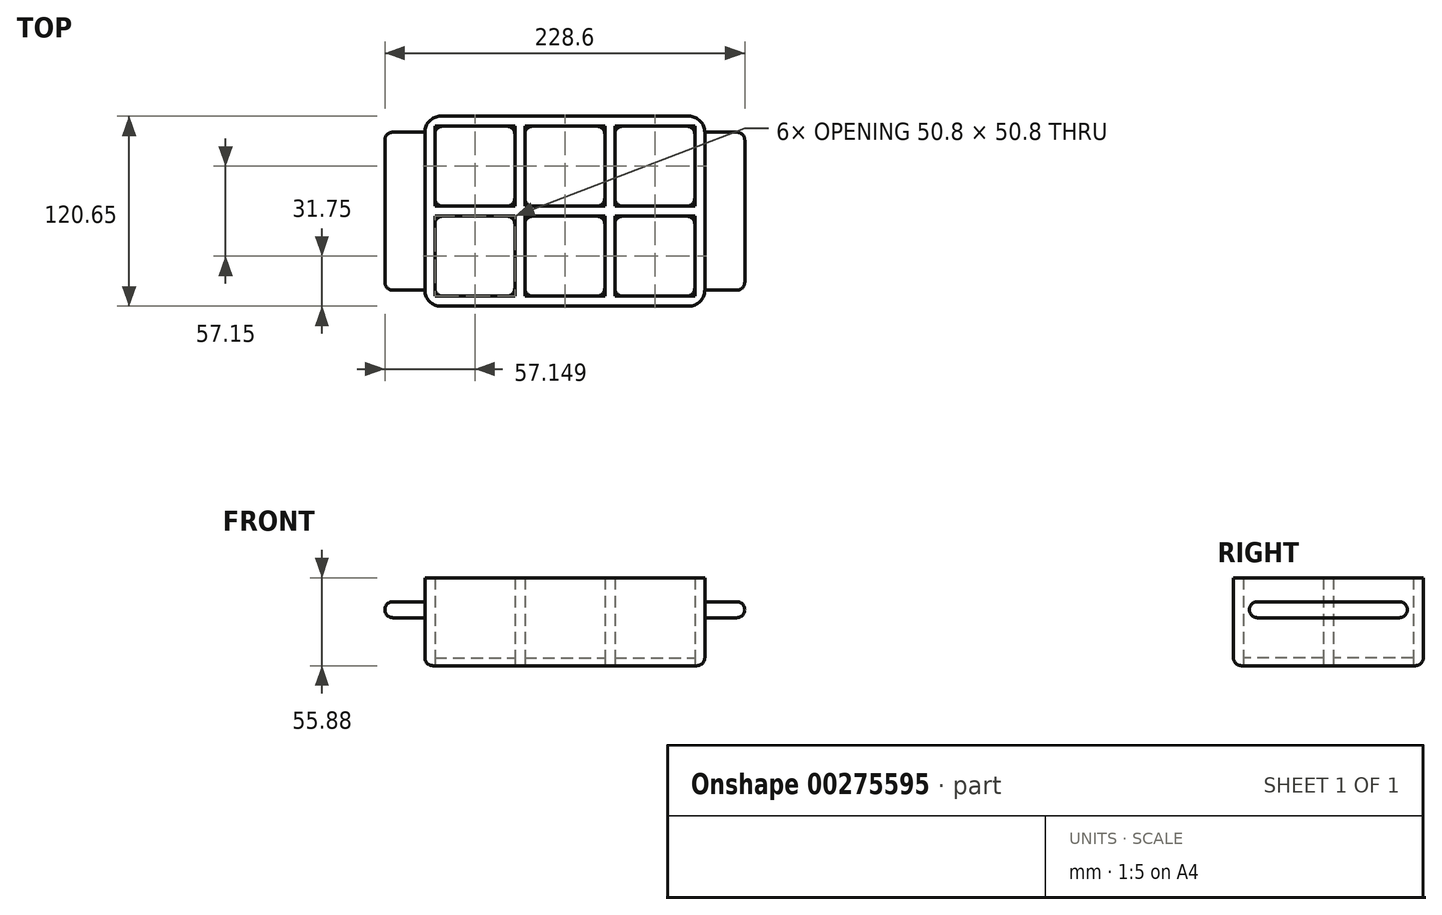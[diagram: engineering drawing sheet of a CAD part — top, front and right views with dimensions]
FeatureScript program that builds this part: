
annotation { "Feature Type Name" : "Feature", "Feature Type Description" : "" }
export const myFeature = defineFeature(function(context is Context, id is Id, definition is map)
    precondition{}
    {
        {
            var Q0;
            Q0=qCreatedBy(makeId("Top.planeOp"),FACE);
            var sketch = newSketch(context, id + "F0", { "sketchPlane" : qUnion([Q0])});
            skLineSegment(sketch, "E0.bottom", {"start": v(-74.45, 57.15) * mm, "end": v(103.35, 57.15) * mm});
            skLineSegment(sketch, "E0.top", {"start": v(-74.45, -63.5) * mm, "end": v(103.35, -63.5) * mm});
            skLineSegment(sketch, "E0.left", {"start": v(-74.45, 57.15) * mm, "end": v(-74.45, -63.5) * mm});
            skLineSegment(sketch, "E0.right", {"start": v(103.35, 57.15) * mm, "end": v(103.35, -63.5) * mm});
            skLineSegment(sketch, "E1.bottom", {"start": v(-68.1, 50.8) * mm, "end": v(-17.3, 50.8) * mm});
            skLineSegment(sketch, "E1.top", {"start": v(-68.1, 0) * mm, "end": v(-17.3, 0) * mm});
            skLineSegment(sketch, "E1.left", {"start": v(-68.1, 50.8) * mm, "end": v(-68.1, 0) * mm});
            skLineSegment(sketch, "E1.right", {"start": v(-17.3, 50.8) * mm, "end": v(-17.3, 0) * mm});
            skLineSegment(sketch, "E2.bottom", {"start": v(-68.1, -6.35) * mm, "end": v(-17.3, -6.35) * mm});
            skLineSegment(sketch, "E2.top", {"start": v(-68.1, -57.15) * mm, "end": v(-17.3, -57.15) * mm});
            skLineSegment(sketch, "E2.left", {"start": v(-68.1, -6.35) * mm, "end": v(-68.1, -57.15) * mm});
            skLineSegment(sketch, "E2.right", {"start": v(-17.3, -6.35) * mm, "end": v(-17.3, -57.15) * mm});
            skLineSegment(sketch, "E3.bottom", {"start": v(-10.95, 50.8) * mm, "end": v(39.85, 50.8) * mm});
            skLineSegment(sketch, "E3.top", {"start": v(-10.95, 0) * mm, "end": v(39.85, 0) * mm});
            skLineSegment(sketch, "E3.left", {"start": v(-10.95, 50.8) * mm, "end": v(-10.95, 0) * mm});
            skLineSegment(sketch, "E3.right", {"start": v(39.85, 50.8) * mm, "end": v(39.85, 0) * mm});
            skLineSegment(sketch, "E4.bottom", {"start": v(-10.95, -6.35) * mm, "end": v(39.85, -6.35) * mm});
            skLineSegment(sketch, "E4.top", {"start": v(-10.95, -57.15) * mm, "end": v(39.85, -57.15) * mm});
            skLineSegment(sketch, "E4.left", {"start": v(-10.95, -6.35) * mm, "end": v(-10.95, -57.15) * mm});
            skLineSegment(sketch, "E4.right", {"start": v(39.85, -6.35) * mm, "end": v(39.85, -57.15) * mm});
            skLineSegment(sketch, "E5.bottom", {"start": v(46.2, 50.8) * mm, "end": v(97, 50.8) * mm});
            skLineSegment(sketch, "E5.top", {"start": v(46.2, 0) * mm, "end": v(97, 0) * mm});
            skLineSegment(sketch, "E5.left", {"start": v(46.2, 50.8) * mm, "end": v(46.2, 0) * mm});
            skLineSegment(sketch, "E5.right", {"start": v(97, 50.8) * mm, "end": v(97, 0) * mm});
            skLineSegment(sketch, "E6.bottom", {"start": v(46.2, -6.35) * mm, "end": v(97, -6.35) * mm});
            skLineSegment(sketch, "E6.top", {"start": v(46.2, -57.15) * mm, "end": v(97, -57.15) * mm});
            skLineSegment(sketch, "E6.left", {"start": v(46.2, -6.35) * mm, "end": v(46.2, -57.15) * mm});
            skLineSegment(sketch, "E6.right", {"start": v(97, -6.35) * mm, "end": v(97, -57.15) * mm});
            skSolve(sketch);
        }
        {
            var Q0;
            Q0=makeQuery(id+"F0.imprint","IMPRINT",FACE,{"disambiguationData":[TD([[makeQuery(id+"F0.imprint","IMPRINT",EDGE,{"derivedFrom":sQuery(id+"F0.wireOp",EDGE,"E6.bottom")}),-1.0]])]});
            var Q1;
            Q1=makeQuery(id+"F0.imprint","IMPRINT",FACE,{"disambiguationData":[TD([[makeQuery(id+"F0.imprint","IMPRINT",EDGE,{"derivedFrom":sQuery(id+"F0.wireOp",EDGE,"E4.bottom")}),-1.0]])]});
            var Q2;
            Q2=makeQuery(id+"F0.imprint","IMPRINT",FACE,{"disambiguationData":[TD([[makeQuery(id+"F0.imprint","IMPRINT",EDGE,{"derivedFrom":sQuery(id+"F0.wireOp",EDGE,"E2.bottom")}),-1.0]])]});
            var Q3;
            Q3=makeQuery(id+"F0.imprint","IMPRINT",FACE,{"disambiguationData":[TD([[makeQuery(id+"F0.imprint","IMPRINT",EDGE,{"derivedFrom":sQuery(id+"F0.wireOp",EDGE,"E1.bottom")}),-1.0]])]});
            var Q4;
            Q4=makeQuery(id+"F0.imprint","IMPRINT",FACE,{"disambiguationData":[TD([[makeQuery(id+"F0.imprint","IMPRINT",EDGE,{"derivedFrom":sQuery(id+"F0.wireOp",EDGE,"E3.bottom")}),-1.0]])]});
            var Q5;
            Q5=makeQuery(id+"F0.imprint","IMPRINT",FACE,{"disambiguationData":[TD([[makeQuery(id+"F0.imprint","IMPRINT",EDGE,{"derivedFrom":sQuery(id+"F0.wireOp",EDGE,"E5.bottom")}),-1.0]])]});
            extrude(context, id + "F1", {"entities" : qUnion([Q0, Q1, Q2, Q3, Q4, Q5]), "depth" : 5.08 * mm});
        }
        {
            var Q0;
            Q0 = qSketchRegion(id + "F0", true);
            extrude(context, id + "F2", {"entities" : qUnion([Q0]), "depth" : 55.88 * mm});
        }
        {
            var Q0;
            Q0=makeQuery(id+"F2.opExtrude","SWEPT_EDGE",EDGE,{"disambiguationData":[OSD([sQuery(id+"F0.wireOp",EDGE,"E0.top"),sQuery(id+"F0.wireOp",EDGE,"E0.right")])]});
            var Q1;
            Q1=makeQuery(id+"F2.opExtrude","SWEPT_EDGE",EDGE,{"disambiguationData":[OSD([sQuery(id+"F0.wireOp",EDGE,"E0.bottom"),sQuery(id+"F0.wireOp",EDGE,"E0.right")])]});
            var Q2;
            Q2=makeQuery(id+"F2.opExtrude","SWEPT_EDGE",EDGE,{"disambiguationData":[OSD([sQuery(id+"F0.wireOp",EDGE,"E0.bottom"),sQuery(id+"F0.wireOp",EDGE,"E0.left")])]});
            var Q3;
            Q3=makeQuery(id+"F2.opExtrude","SWEPT_EDGE",EDGE,{"disambiguationData":[OSD([sQuery(id+"F0.wireOp",EDGE,"E0.top"),sQuery(id+"F0.wireOp",EDGE,"E0.left")])]});
            fillet(context, id + "F3", {"entities" : qUnion([Q0, Q1, Q2, Q3]), "radius" : 10.16 * mm, "tangentPropagation" : true, "allowEdgeOverflow" : false});
        }
        {
            var Q0;
            Q0=makeQuery(id+"F2.opExtrude","SWEPT_EDGE",EDGE,{"disambiguationData":[OSD([sQuery(id+"F0.wireOp",EDGE,"E2.bottom"),sQuery(id+"F0.wireOp",EDGE,"E2.right")])]});
            var Q1;
            Q1=makeQuery(id+"F2.opExtrude","SWEPT_EDGE",EDGE,{"disambiguationData":[OSD([sQuery(id+"F0.wireOp",EDGE,"E1.bottom"),sQuery(id+"F0.wireOp",EDGE,"E1.right")])]});
            var Q2;
            Q2=makeQuery(id+"F2.opExtrude","SWEPT_EDGE",EDGE,{"disambiguationData":[OSD([sQuery(id+"F0.wireOp",EDGE,"E3.bottom"),sQuery(id+"F0.wireOp",EDGE,"E3.right")])]});
            var Q3;
            Q3=makeQuery(id+"F2.opExtrude","SWEPT_EDGE",EDGE,{"disambiguationData":[OSD([sQuery(id+"F0.wireOp",EDGE,"E5.bottom"),sQuery(id+"F0.wireOp",EDGE,"E5.right")])]});
            var Q4;
            Q4=makeQuery(id+"F2.opExtrude","SWEPT_EDGE",EDGE,{"disambiguationData":[OSD([sQuery(id+"F0.wireOp",EDGE,"E6.bottom"),sQuery(id+"F0.wireOp",EDGE,"E6.right")])]});
            var Q5;
            Q5=makeQuery(id+"F2.opExtrude","SWEPT_EDGE",EDGE,{"disambiguationData":[OSD([sQuery(id+"F0.wireOp",EDGE,"E4.bottom"),sQuery(id+"F0.wireOp",EDGE,"E4.right")])]});
            var Q6;
            Q6=makeQuery(id+"F2.opExtrude","SWEPT_EDGE",EDGE,{"disambiguationData":[OSD([sQuery(id+"F0.wireOp",EDGE,"E5.top"),sQuery(id+"F0.wireOp",EDGE,"E5.right")])]});
            var Q7;
            Q7=makeQuery(id+"F2.opExtrude","SWEPT_EDGE",EDGE,{"disambiguationData":[OSD([sQuery(id+"F0.wireOp",EDGE,"E3.top"),sQuery(id+"F0.wireOp",EDGE,"E3.right")])]});
            var Q8;
            Q8=makeQuery(id+"F2.opExtrude","SWEPT_EDGE",EDGE,{"disambiguationData":[OSD([sQuery(id+"F0.wireOp",EDGE,"E1.top"),sQuery(id+"F0.wireOp",EDGE,"E1.right")])]});
            var Q9;
            Q9=makeQuery(id+"F2.opExtrude","SWEPT_EDGE",EDGE,{"disambiguationData":[OSD([sQuery(id+"F0.wireOp",EDGE,"E2.top"),sQuery(id+"F0.wireOp",EDGE,"E2.right")])]});
            var Q10;
            Q10=makeQuery(id+"F2.opExtrude","SWEPT_EDGE",EDGE,{"disambiguationData":[OSD([sQuery(id+"F0.wireOp",EDGE,"E4.top"),sQuery(id+"F0.wireOp",EDGE,"E4.right")])]});
            var Q11;
            Q11=makeQuery(id+"F2.opExtrude","SWEPT_EDGE",EDGE,{"disambiguationData":[OSD([sQuery(id+"F0.wireOp",EDGE,"E6.top"),sQuery(id+"F0.wireOp",EDGE,"E6.right")])]});
            var Q12;
            Q12=makeQuery(id+"F2.opExtrude","SWEPT_EDGE",EDGE,{"disambiguationData":[OSD([sQuery(id+"F0.wireOp",EDGE,"E6.top"),sQuery(id+"F0.wireOp",EDGE,"E6.left")])]});
            var Q13;
            Q13=makeQuery(id+"F2.opExtrude","SWEPT_EDGE",EDGE,{"disambiguationData":[OSD([sQuery(id+"F0.wireOp",EDGE,"E5.top"),sQuery(id+"F0.wireOp",EDGE,"E5.left")])]});
            var Q14;
            Q14=makeQuery(id+"F2.opExtrude","SWEPT_EDGE",EDGE,{"disambiguationData":[OSD([sQuery(id+"F0.wireOp",EDGE,"E4.top"),sQuery(id+"F0.wireOp",EDGE,"E4.left")])]});
            var Q15;
            Q15=makeQuery(id+"F2.opExtrude","SWEPT_EDGE",EDGE,{"disambiguationData":[OSD([sQuery(id+"F0.wireOp",EDGE,"E3.top"),sQuery(id+"F0.wireOp",EDGE,"E3.left")])]});
            var Q16;
            Q16=makeQuery(id+"F2.opExtrude","SWEPT_EDGE",EDGE,{"disambiguationData":[OSD([sQuery(id+"F0.wireOp",EDGE,"E1.top"),sQuery(id+"F0.wireOp",EDGE,"E1.left")])]});
            var Q17;
            Q17=makeQuery(id+"F2.opExtrude","SWEPT_EDGE",EDGE,{"disambiguationData":[OSD([sQuery(id+"F0.wireOp",EDGE,"E2.top"),sQuery(id+"F0.wireOp",EDGE,"E2.left")])]});
            var Q18;
            Q18=makeQuery(id+"F2.opExtrude","SWEPT_EDGE",EDGE,{"disambiguationData":[OSD([sQuery(id+"F0.wireOp",EDGE,"E6.bottom"),sQuery(id+"F0.wireOp",EDGE,"E6.left")])]});
            var Q19;
            Q19=makeQuery(id+"F2.opExtrude","SWEPT_EDGE",EDGE,{"disambiguationData":[OSD([sQuery(id+"F0.wireOp",EDGE,"E5.bottom"),sQuery(id+"F0.wireOp",EDGE,"E5.left")])]});
            var Q20;
            Q20=makeQuery(id+"F2.opExtrude","SWEPT_EDGE",EDGE,{"disambiguationData":[OSD([sQuery(id+"F0.wireOp",EDGE,"E3.bottom"),sQuery(id+"F0.wireOp",EDGE,"E3.left")])]});
            var Q21;
            Q21=makeQuery(id+"F2.opExtrude","SWEPT_EDGE",EDGE,{"disambiguationData":[OSD([sQuery(id+"F0.wireOp",EDGE,"E4.bottom"),sQuery(id+"F0.wireOp",EDGE,"E4.left")])]});
            var Q22;
            Q22=makeQuery(id+"F2.opExtrude","SWEPT_EDGE",EDGE,{"disambiguationData":[OSD([sQuery(id+"F0.wireOp",EDGE,"E2.bottom"),sQuery(id+"F0.wireOp",EDGE,"E2.left")])]});
            var Q23;
            Q23=makeQuery(id+"F2.opExtrude","SWEPT_EDGE",EDGE,{"disambiguationData":[OSD([sQuery(id+"F0.wireOp",EDGE,"E1.bottom"),sQuery(id+"F0.wireOp",EDGE,"E1.left")])]});
            var Q24;
            Q24=makeQuery(id+"F2.opExtrude","CAP_EDGE",EDGE,{"disambiguationData":[OSD([sQuery(id+"F0.wireOp",EDGE,"E0.right")])],"isStart":true});
            var Q25;
            Q25=makeQuery(id+"F2.opExtrude","CAP_EDGE",EDGE,{"disambiguationData":[OSD([sQuery(id+"F0.wireOp",EDGE,"E0.top")])],"isStart":true});
            fillet(context, id + "F4", {"entities" : qUnion([Q0, Q1, Q2, Q3, Q4, Q5, Q6, Q7, Q8, Q9, Q10, Q11, Q12, Q13, Q14, Q15, Q16, Q17, Q18, Q19, Q20, Q21, Q22, Q23, Q24, Q25]), "radius" : 5.08 * mm, "tangentPropagation" : true, "allowEdgeOverflow" : false});
        }
        {
            var Q0;
            Q0=makeQuery(id+"F2.opExtrude","SWEPT_FACE",FACE,{"disambiguationData":[OSD([sQuery(id+"F0.wireOp",EDGE,"E0.right")])]});
            var sketch = newSketch(context, id + "F5", { "sketchPlane" : qUnion([Q0])});
            skLineSegment(sketch, "E7.bottom", {"start": v(-53.34, 30.48) * mm, "end": v(47, 30.48) * mm});
            skLineSegment(sketch, "E7.top", {"start": v(-53.34, 40.64) * mm, "end": v(47, 40.64) * mm});
            skLineSegment(sketch, "E7.left", {"start": v(-53.34, 30.48) * mm, "end": v(-53.34, 40.64) * mm});
            skLineSegment(sketch, "E7.right", {"start": v(46.99, 30.48) * mm, "end": v(46.99, 40.64) * mm});
            skSolve(sketch);
        }
        {
            var Q0;
            Q0=makeQuery(id+"F5.imprint","IMPRINT",FACE,{"disambiguationData":[TD([[makeQuery(id+"F5.imprint","IMPRINT",EDGE,{"derivedFrom":sQuery(id+"F5.wireOp",EDGE,"E7.bottom")}),1.0]])]});
            extrude(context, id + "F6", {"entities" : qUnion([Q0]), "operationType" : NewBodyOperationType.ADD, "depth" : 25.4 * mm});
        }
        {
            var Q0;
            Q0=makeQuery(id+"F6.opExtrude","CAP_EDGE",EDGE,{"disambiguationData":[OSD([sQuery(id+"F5.wireOp",EDGE,"E7.top")])],"isStart":false});
            var Q1;
            Q1=makeQuery(id+"F6.opExtrude","SWEPT_EDGE",EDGE,{"disambiguationData":[OSD([sQuery(id+"F0.wireOp",EDGE,"E0.top"),sQuery(id+"F0.wireOp",EDGE,"E0.right"),sQuery(id+"F5.wireOp",EDGE,"E7.top"),sQuery(id+"F5.wireOp",EDGE,"E7.left")])]});
            var Q2;
            Q2=makeQuery(id+"F6.opExtrude","CAP_EDGE",EDGE,{"disambiguationData":[OSD([sQuery(id+"F5.wireOp",EDGE,"E7.left")])],"isStart":false});
            var Q3;
            Q3=makeQuery(id+"F6.opExtrude","SWEPT_EDGE",EDGE,{"disambiguationData":[OSD([sQuery(id+"F0.wireOp",EDGE,"E0.top"),sQuery(id+"F0.wireOp",EDGE,"E0.right"),sQuery(id+"F5.wireOp",EDGE,"E7.bottom"),sQuery(id+"F5.wireOp",EDGE,"E7.left")])]});
            var Q4;
            Q4=makeQuery(id+"F6.opExtrude","CAP_EDGE",EDGE,{"disambiguationData":[OSD([sQuery(id+"F5.wireOp",EDGE,"E7.bottom")])],"isStart":false});
            var Q5;
            Q5=makeQuery(id+"F6.opExtrude","SWEPT_EDGE",EDGE,{"disambiguationData":[OSD([sQuery(id+"F0.wireOp",EDGE,"E0.bottom"),sQuery(id+"F0.wireOp",EDGE,"E0.right"),sQuery(id+"F5.wireOp",EDGE,"E7.top"),sQuery(id+"F5.wireOp",EDGE,"E7.right")])]});
            var Q6;
            Q6=makeQuery(id+"F6.opExtrude","SWEPT_EDGE",EDGE,{"disambiguationData":[OSD([sQuery(id+"F0.wireOp",EDGE,"E0.bottom"),sQuery(id+"F0.wireOp",EDGE,"E0.right"),sQuery(id+"F5.wireOp",EDGE,"E7.bottom"),sQuery(id+"F5.wireOp",EDGE,"E7.right")])]});
            var Q7;
            Q7=makeQuery(id+"F6.opExtrude","CAP_EDGE",EDGE,{"disambiguationData":[OSD([sQuery(id+"F5.wireOp",EDGE,"E7.right")])],"isStart":false});
            fillet(context, id + "F7", {"entities" : qUnion([Q0, Q1, Q2, Q3, Q4, Q5, Q6, Q7]), "radius" : 5.08 * mm, "tangentPropagation" : true, "allowEdgeOverflow" : false});
        }
        {
            var Q0;
            Q0=makeQuery(id+"F2.opExtrude","SWEPT_FACE",FACE,{"disambiguationData":[OSD([sQuery(id+"F0.wireOp",EDGE,"E0.left")])]});
            var sketch = newSketch(context, id + "F8", { "sketchPlane" : qUnion([Q0])});
            skLineSegment(sketch, "E8.bottom", {"start": v(-47, 30.48) * mm, "end": v(53.34, 30.48) * mm});
            skLineSegment(sketch, "E8.top", {"start": v(-47, 40.64) * mm, "end": v(53.34, 40.64) * mm});
            skLineSegment(sketch, "E8.left", {"start": v(-47, 30.48) * mm, "end": v(-47, 40.64) * mm});
            skLineSegment(sketch, "E8.right", {"start": v(53.34, 30.48) * mm, "end": v(53.34, 40.64) * mm});
            skSolve(sketch);
        }
        {
            var Q0;
            Q0=makeQuery(id+"F8.imprint","IMPRINT",FACE,{"disambiguationData":[TD([[makeQuery(id+"F8.imprint","IMPRINT",EDGE,{"derivedFrom":sQuery(id+"F8.wireOp",EDGE,"E8.bottom")}),1.0]])]});
            extrude(context, id + "F9", {"entities" : qUnion([Q0]), "operationType" : NewBodyOperationType.ADD, "depth" : 25.4 * mm});
        }
        {
            var Q0;
            Q0=makeQuery(id+"F9.opExtrude","CAP_EDGE",EDGE,{"disambiguationData":[OSD([sQuery(id+"F8.wireOp",EDGE,"E8.top")])],"isStart":false});
            var Q1;
            Q1=makeQuery(id+"F9.opExtrude","CAP_EDGE",EDGE,{"disambiguationData":[OSD([sQuery(id+"F8.wireOp",EDGE,"E8.bottom")])],"isStart":false});
            var Q2;
            Q2=makeQuery(id+"F9.opExtrude","CAP_EDGE",EDGE,{"disambiguationData":[OSD([sQuery(id+"F8.wireOp",EDGE,"E8.right")])],"isStart":false});
            var Q3;
            Q3=makeQuery(id+"F9.opExtrude","SWEPT_EDGE",EDGE,{"disambiguationData":[OSD([sQuery(id+"F0.wireOp",EDGE,"E0.top"),sQuery(id+"F0.wireOp",EDGE,"E0.left"),sQuery(id+"F8.wireOp",EDGE,"E8.top"),sQuery(id+"F8.wireOp",EDGE,"E8.right")])]});
            var Q4;
            Q4=makeQuery(id+"F9.opExtrude","SWEPT_EDGE",EDGE,{"disambiguationData":[OSD([sQuery(id+"F0.wireOp",EDGE,"E0.top"),sQuery(id+"F0.wireOp",EDGE,"E0.left"),sQuery(id+"F8.wireOp",EDGE,"E8.bottom"),sQuery(id+"F8.wireOp",EDGE,"E8.right")])]});
            var Q5;
            Q5=makeQuery(id+"F9.opExtrude","SWEPT_EDGE",EDGE,{"disambiguationData":[OSD([sQuery(id+"F0.wireOp",EDGE,"E0.bottom"),sQuery(id+"F0.wireOp",EDGE,"E0.left"),sQuery(id+"F8.wireOp",EDGE,"E8.bottom"),sQuery(id+"F8.wireOp",EDGE,"E8.left")])]});
            var Q6;
            Q6=makeQuery(id+"F9.opExtrude","SWEPT_EDGE",EDGE,{"disambiguationData":[OSD([sQuery(id+"F0.wireOp",EDGE,"E0.bottom"),sQuery(id+"F0.wireOp",EDGE,"E0.left"),sQuery(id+"F8.wireOp",EDGE,"E8.top"),sQuery(id+"F8.wireOp",EDGE,"E8.left")])]});
            var Q7;
            Q7=makeQuery(id+"F9.opExtrude","CAP_EDGE",EDGE,{"disambiguationData":[OSD([sQuery(id+"F8.wireOp",EDGE,"E8.left")])],"isStart":false});
            fillet(context, id + "F10", {"entities" : qUnion([Q0, Q1, Q2, Q3, Q4, Q5, Q6, Q7]), "radius" : 5.08 * mm, "tangentPropagation" : true, "allowEdgeOverflow" : false});
        }
    });
